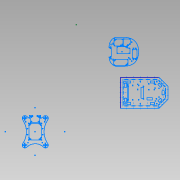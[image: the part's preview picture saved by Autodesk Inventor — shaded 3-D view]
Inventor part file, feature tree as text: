
AUTODESK INVENTOR PART (.ipt)
format: ipt  version: 2015 SP1 (Build 190203100, 203)  size: 231,936 bytes
history: native  units: mm
features: sketch x1
ambient origin geometry x8: Origin, YZ Plane, XZ Plane, XY Plane, X Axis, Y Axis, Z Axis, Center Point
feature tree (1):
  sketch  "Sketch1"  dims[d104=30.0mm d106=23.0mm d107=30.0mm d109=23.0mm d113=30.0mm d115=32.5mm d116=30.0mm d118=32.5mm d121=172.234468mm d123=172.234468mm d124=58.326098mm d125=58.326098mm d126=58.326098mm d127=23.561995mm d128=23.561874mm d129=23.562018mm d130=23.561892mm d131=15.707985mm d132=15.707942mm d133=10.0mm d134=10.0mm d135=9.999879mm d136=10.0mm d137=10.0mm d138=10.0mm d143=140.811657mm]
